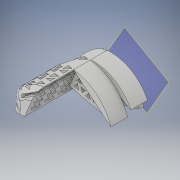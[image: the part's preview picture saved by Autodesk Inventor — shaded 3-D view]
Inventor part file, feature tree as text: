
AUTODESK INVENTOR PART (.ipt)
format: ipt  version: 2017 (Build 210142000, 142)  size: 984,576 bytes
history: native  units: mm
features: sketch x27, extrude x23, plane x7, fillet x6, other x3, boolean_combine x1, revolve x1, sweep x1
ambient origin geometry x8: Origin, YZ Plane, XZ Plane, XY Plane, X Axis, Y Axis, Z Axis, Center Point
bodies: Solid1 (feature_tree), Solid2 (feature_tree), Solid3 (feature_tree), Solid4 (feature_tree), Solid5 (feature_tree)
feature tree (69):
  extrude  "Extrusion1"  Depth=35.0mm
  plane  "Work Plane1"
  extrude  "Extrusion2"  Depth=33.005mm
  extrude  "Extrusion3"  TaperAngle=0.0deg  [1 undecoded]
  plane  "Work Plane2"
  extrude  "Extrusion4"  Depth=20.0mm
  other  "Work Axis1"
  extrude  "Extrusion5"  Depth=10.0mm
  sketch  "Sketch6"  dims[d12=48.556624mm d13=20.0mm d14=0.0mm]
  boolean_combine  "Combine1"
  extrude  "Extrusion6"  Depth=20.0mm TaperAngle=0.0deg
  extrude  "Extrusion7"  Depth=20.0mm TaperAngle=0.0deg
  other  "Work Axis2"
  fillet  "Fillet1"  Radius=53.287466mm
  revolve  "Revolution1"  [1 undecoded]
  extrude  "Extrusion8"  Depth=20.0mm
  sketch  "Sketch10"  dims[d25=7.433428mm d26=13.25mm d27=0.0mm]
  plane  "Work Plane3"
  sweep  "Sweep1"
  extrude  "Extrusion9"  TaperAngle=90.0deg  [1 undecoded]
  fillet  "Fillet2"  Radius=40.197898mm
  extrude  "Extrusion10"  Depth=15.060899mm
  extrude  "Extrusion11"  Depth=10.650813mm
  extrude  "Extrusion12"  Depth=5.3475mm
  fillet  "Fillet3"  Radius=15.0mm
  fillet  "Fillet4"  [1 undecoded]
  fillet  "Fillet5"  Radius=27.295196mm
  other  "Bend Part1"
  extrude  "Extrusion13"  Depth=20.0mm
  plane  "Work Plane4"
  extrude  "Extrusion14"  TaperAngle=0.0deg  [1 undecoded]
  fillet  "Fillet6"  Radius=13.25mm
  extrude  "Extrusion15"  Depth=10.0mm TaperAngle=0.0deg
  plane  "Work Plane5"
  extrude  "Extrusion16"  Depth=10.0mm
  extrude  "Extrusion22"  Depth=10.0mm TaperAngle=0.0deg
  extrude  "Extrusion23"  Depth=10.0mm
  extrude  "Extrusion24"  Depth=10.0mm TaperAngle=180.0deg
  extrude  "Extrusion25"  Depth=18.153275mm
  plane  "Work Plane7"
  extrude  "Extrusion26"  TaperAngle=90.0deg  [1 undecoded]
  extrude  "Extrusion27"  Depth=57.396209mm
  extrude  "Extrusion28"  Depth=2.0mm
  plane  "Work Plane8"
  sketch  "Sketch1"  dims[d0=60.0mm d1=35.0mm]
  sketch  "Sketch2"  dims[d2=60.0mm d3=33.005mm]
  sketch  "Sketch3"  dims[d4=75.0mm d5=0.0mm d6=0.0mm]
  sketch  "Sketch4"  dims[d7=35.0mm d8=20.0mm]
  sketch  "Sketch5"  dims[d9=55.0mm d10=0.0mm d11=10.0mm]
  sketch  "Sketch7"  dims[d15=90.0deg d16=20.0mm d17=0.0mm d18=53.287466mm]
  sketch  "Sketch8"  dims[d19=20.0mm d20=0.0mm d21=14.476257mm]
  sketch  "Sketch9"  dims[d22=20.0mm d23=0.0mm d24=61.358233mm]
  sketch  "Sketch11"  dims[d28=10.0mm d29=90.0deg d30=40.197898mm]
  sketch  "Sketch12"  dims[d31=90.965929mm d32=15.060899mm]
  sketch  "Sketch13"  dims[d33=0.0mm d34=0.0mm d35=10.650813mm]
  sketch  "Sketch15"  dims[d36=90.0deg d37=5.3475mm d38=15.0mm d39=45.0deg d40=27.295196mm]
  sketch  "Sketch16"  dims[d41=20.0mm d42=5.348mm]
  sketch  "Sketch18"  dims[d43=60.0mm d44=0.0mm d45=0.0mm d46=13.25mm d47=0.0mm]
  sketch  "Sketch19"  dims[d48=10.0mm d49=75.0mm d50=0.0mm]
  sketch  "Sketch20"  dims[d52=10.0mm d53=10.80569mm]
  sketch  "Sketch21"  dims[d54=10.0mm d55=0.0mm d56=4.8mm d57=0.0mm]
  sketch  "Sketch22"  dims[d58=10.0mm d59=10.0mm]
  sketch  "Sketch28"  dims[d60=10.0mm d62=2.0mm d63=180.0deg]
  sketch  "Sketch29"  dims[d64=18.153275mm d65=18.153275mm]
  sketch  "Sketch30"  dims[d66=75.0mm d67=0.0mm d68=90.0deg]
  sketch  "Sketch31"  dims[d69=75.0mm d70=57.396209mm]
  sketch  "Sketch32"  dims[d71=75.0mm d72=0.0mm d73=2.0mm]
  sketch  "Sketch33"  dims[d74=27.7545mm]
  sketch  "Sketch34"  dims[d75=17.5mm d76=5.0mm d77=0.0mm d78=20.0mm d79=28.8585mm d80=10.0mm d81=0.0mm d108=10.0mm d109=0.0mm d110=5.0mm d111=0.0mm d112=20.0mm d113=3.0mm d114=2.5mm d115=19.198622mm d116=10.0mm d117=0.0mm d118=20.0mm d119=3.0mm d120=13.189mm d121=20.0mm d122=3.0mm d123=11.073mm d124=10.0mm d125=5.0mm d126=0.0mm d127=0.0mm d128=5.202827mm d129=2.5mm d130=20.0mm d131=47.662mm d132=0.0mm d133=6.0mm d134=4.0mm d136=4.0mm d137=6.0mm d138=4.0mm d140=4.0mm d141=30.0mm d143=16.0mm d144=30.0mm d146=8.0mm d149=20.0mm d151=19.0mm d152=10.0mm d154=10.0mm d156=20.0mm d158=8.0mm d159=10.0mm d161=10.0mm d163=0.0mm d164=0.0mm d165=6.0mm d166=4.0mm d167=4.0mm d168=6.0mm d169=4.0mm d170=4.0mm d171=20.0mm d173=14.0mm d174=20.0mm d176=8.0mm d179=10.0mm d180=0.0mm d181=10.0mm]
note: 6 required parameter values undecoded (feature->parameter linkage not recoverable at this tier; creation-order binding heuristic only, values carry confidence <= 0.55)